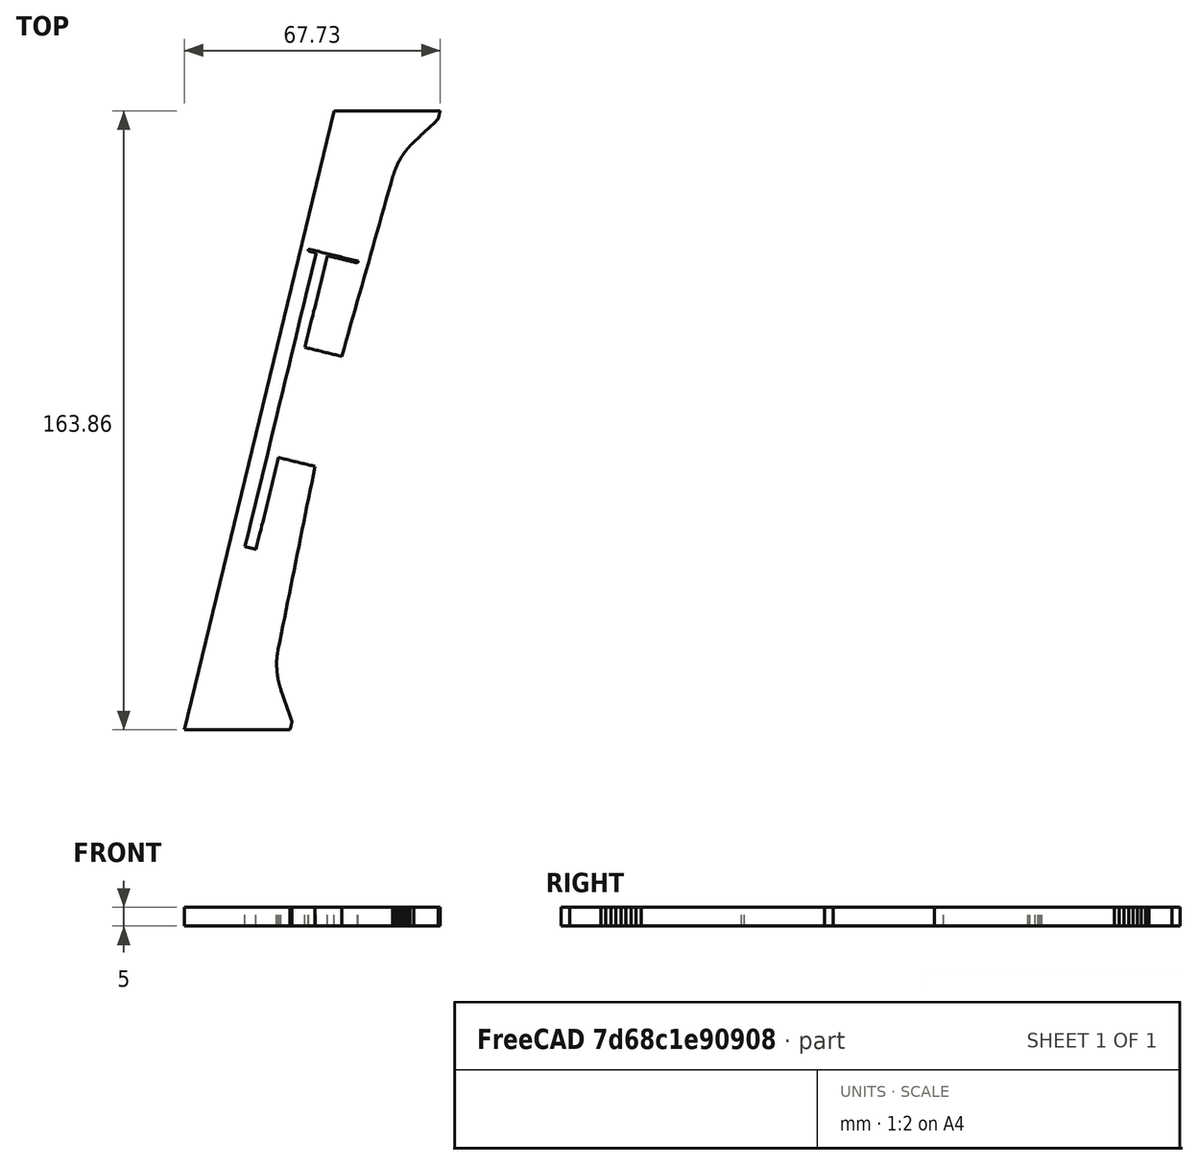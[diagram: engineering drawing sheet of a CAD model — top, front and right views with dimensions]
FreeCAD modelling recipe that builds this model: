
FCSTD DOCUMENT  (FreeCAD 0.19R)
Label: F-35_v2_parts_14
License: All rights reserved
LicenseURL: http://en.wikipedia.org/wiki/All_rights_reserved
objects: App::DocumentObjectGroup×2, PartDesign::CoordinateSystem×2, App::FeaturePython×1, Sketcher::SketchObject×1, PartDesign::Pad×1, PartDesign::Body×1, App::Part×1
note: 6 computed .brp shape members not serialized (recipe doc carries the construction recipe); baked Part::Feature solids carry a one-line shape summary decoded from their .brp

FEATURE [App::DocumentObjectGroup] Parts
FEATURE [PartDesign::CoordinateSystem] LCS_Origin
  AttacherType = Attacher::AttachEngine3D
  MapMode = 2
  Support = -> [X_Axis]
FEATURE [App::DocumentObjectGroup] Constraints
FEATURE [App::FeaturePython] Variables  # WARN: FeaturePython — macro-defined, semantics opaque (R4)
FEATURE [Sketcher::SketchObject] Sketch001
  FullyConstrained = false
  sketch-geometry (36):
    g0: BSplineCurve PolesCount=2 KnotsCount=2 Degree=1 IsPeriodic=0
    g1: BSplineCurve PolesCount=2 KnotsCount=2 Degree=1 IsPeriodic=0
    g2: BSplineCurve PolesCount=2 KnotsCount=2 Degree=1 IsPeriodic=0
    g3: BSplineCurve PolesCount=2 KnotsCount=2 Degree=1 IsPeriodic=0
    g4: BSplineCurve PolesCount=2 KnotsCount=2 Degree=1 IsPeriodic=0
    g5: BSplineCurve PolesCount=2 KnotsCount=2 Degree=1 IsPeriodic=0
    g6: BSplineCurve PolesCount=2 KnotsCount=2 Degree=1 IsPeriodic=0
    g7: BSplineCurve PolesCount=2 KnotsCount=2 Degree=1 IsPeriodic=0
    g8: BSplineCurve PolesCount=2 KnotsCount=2 Degree=1 IsPeriodic=0
    g9: BSplineCurve PolesCount=2 KnotsCount=2 Degree=1 IsPeriodic=0
    g10: BSplineCurve PolesCount=2 KnotsCount=2 Degree=1 IsPeriodic=0
    g11: BSplineCurve PolesCount=2 KnotsCount=2 Degree=1 IsPeriodic=0
    g12: BSplineCurve PolesCount=2 KnotsCount=2 Degree=1 IsPeriodic=0
    g13: BSplineCurve PolesCount=2 KnotsCount=2 Degree=1 IsPeriodic=0
    g14: BSplineCurve PolesCount=2 KnotsCount=2 Degree=1 IsPeriodic=0
    g15: BSplineCurve PolesCount=2 KnotsCount=2 Degree=1 IsPeriodic=0
    g16: BSplineCurve PolesCount=2 KnotsCount=2 Degree=1 IsPeriodic=0
    g17: BSplineCurve PolesCount=2 KnotsCount=2 Degree=1 IsPeriodic=0
    g18: BSplineCurve PolesCount=2 KnotsCount=2 Degree=1 IsPeriodic=0
    g19: BSplineCurve PolesCount=2 KnotsCount=2 Degree=1 IsPeriodic=0
    g20: BSplineCurve PolesCount=2 KnotsCount=2 Degree=1 IsPeriodic=0
    g21: BSplineCurve PolesCount=2 KnotsCount=2 Degree=1 IsPeriodic=0
    g22: BSplineCurve PolesCount=2 KnotsCount=2 Degree=1 IsPeriodic=0
    g23: BSplineCurve PolesCount=2 KnotsCount=2 Degree=1 IsPeriodic=0
    g24: BSplineCurve PolesCount=2 KnotsCount=2 Degree=1 IsPeriodic=0
    g25: BSplineCurve PolesCount=2 KnotsCount=2 Degree=1 IsPeriodic=0
    g26: BSplineCurve PolesCount=2 KnotsCount=2 Degree=1 IsPeriodic=0
    g27: BSplineCurve PolesCount=2 KnotsCount=2 Degree=1 IsPeriodic=0
    g28: BSplineCurve PolesCount=2 KnotsCount=2 Degree=1 IsPeriodic=0
    g29: BSplineCurve PolesCount=2 KnotsCount=2 Degree=1 IsPeriodic=0
    g30: BSplineCurve PolesCount=2 KnotsCount=2 Degree=1 IsPeriodic=0
    g31: BSplineCurve PolesCount=2 KnotsCount=2 Degree=1 IsPeriodic=0
    g32: BSplineCurve PolesCount=2 KnotsCount=2 Degree=1 IsPeriodic=0
    g33: BSplineCurve PolesCount=2 KnotsCount=2 Degree=1 IsPeriodic=0
    g34: BSplineCurve PolesCount=2 KnotsCount=2 Degree=1 IsPeriodic=0
    g35: LineSegment StartX=748.511 StartY=-199.265 StartZ=0 EndX=708.789 EndY=-363.131 EndZ=0
  constraints (16):
    c: Coincident(g11,g12)
    c: Coincident(g12,g13)
    c: Coincident(g13,g14)
    c: Coincident(g14,g15)
    c: Coincident(g15,g16)
    c: Coincident(g16,g17)
    c: Coincident(g17,g18)
    c: Coincident(g27,g28)
    c: Coincident(g28,g29)
    c: Coincident(g29,g30)
    c: Coincident(g30,g31)
    c: Coincident(g31,g32)
    c: Coincident(g32,g33)
    c: Coincident(g33,g34)
    c: Coincident(g7,g35)
    c: Coincident(g8,g35)
FEATURE [PartDesign::Pad] Pad005
  Direction = (1,1,1)
  Length = 5
  Length2 = 100
  Profile = -> Sketch001
  Type = 0
FEATURE [PartDesign::Body] Body001  label="Part14"
  Group = -> [Sketch001,Pad005]
  Origin = -> Origin002
  Tip = -> Pad005
FEATURE [PartDesign::CoordinateSystem] LCS_1
  AttacherType = Attacher::AttachEngine3D
  MapMode = 7
  Placement = pos=(748.511,-199.265,5) rot=(0.084182,0.704597,0.704597;2.97363rad)
  Support = -> [Pad005]
FEATURE [App::Part] Model
  Configuration = 0
  Group = -> [LCS_Origin,Constraints,Variables,Body001,LCS_1]
  Origin = -> Origin
  Type = Assembly4 Model
